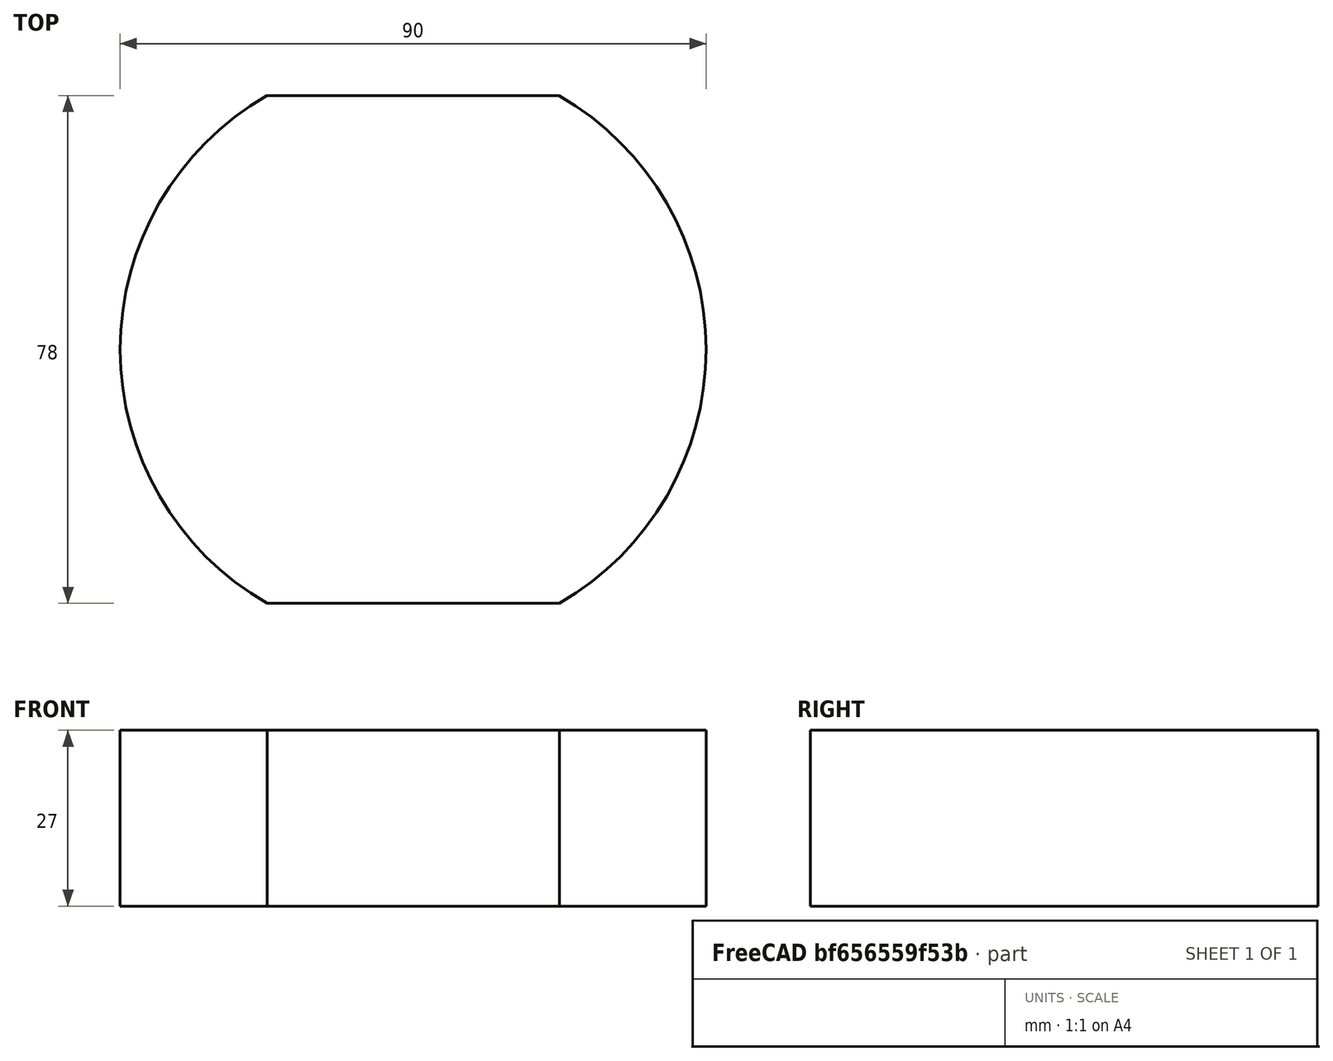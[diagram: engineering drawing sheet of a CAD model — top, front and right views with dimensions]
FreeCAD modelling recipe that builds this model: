
FCSTD DOCUMENT  (FreeCAD 1.0R39319 (Git))
Label: chapa_circle_90mm
License: All rights reserved
LicenseURL: https://en.wikipedia.org/wiki/All_rights_reserved
objects: Sketcher::SketchObject×1, PartDesign::Pad×1, PartDesign::Body×1
note: 6 computed .brp shape members not serialized (recipe doc carries the construction recipe); baked Part::Feature solids carry a one-line shape summary decoded from their .brp

FEATURE [Sketcher::SketchObject] Sketch_1
  ArcFitTolerance = 1e-06
  AttachmentSupport = -> [XY_Plane]
  FullyConstrained = false
  MakeInternals = false
  MapMode = 5
  sketch-geometry (4):
    g0: ArcOfCircle CenterX=0 CenterY=-0.00517858 CenterZ=0 NormalX=0 NormalY=0 NormalZ=1 AngleXU=0 Radius=44.9955 StartAngle=5.23476 EndAngle=7.33207
    g1: LineSegment StartX=22.4319 StartY=39 StartZ=0 EndX=-22.4499 EndY=39 EndZ=0
    g2: ArcOfCircle CenterX=0 CenterY=0.0051765 CenterZ=0 NormalX=0 NormalY=0 NormalZ=1 AngleXU=0 Radius=44.9955 StartAngle=2.09317 EndAngle=4.19048
    g3: LineSegment StartX=-22.4319 StartY=-39 StartZ=0 EndX=22.4499 EndY=-39 EndZ=0
  constraints (7):
    c: Coincident(g0,g1)
    c: Coincident(g1,g2)
    c: Coincident(g2,g3)
    c: Coincident(g3,g0)
    c: Parallel(g1,g3)
    c: Horizontal(g1)
    c: Distance(g1,g3) = 78
FEATURE [PartDesign::Pad] Pad_1
  Direction = (0,0,1)
  Length = 27
  Length2 = 10
  Profile = -> Sketch_1
  Refine = true
  Suppressed = false
  Type = 0
FEATURE [PartDesign::Body] Body
  AllowCompound = false
  Group = -> [Sketch_1,Pad_1]
  Origin = -> Origin
  Tip = -> Pad_1
